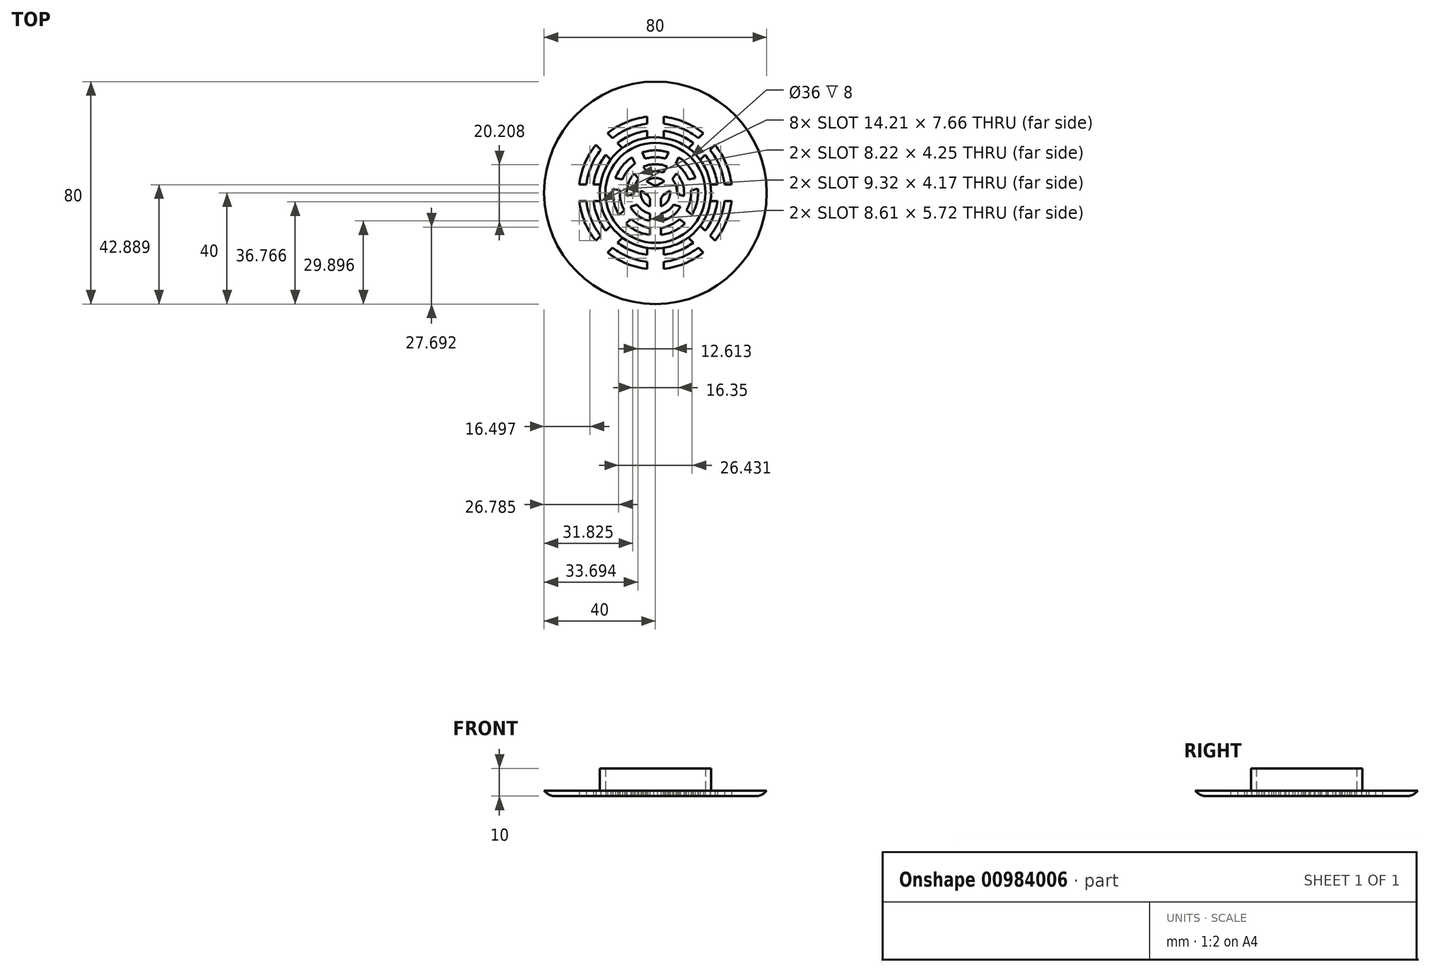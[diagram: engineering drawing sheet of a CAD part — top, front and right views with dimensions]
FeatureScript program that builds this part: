
annotation { "Feature Type Name" : "Feature", "Feature Type Description" : "" }
export const myFeature = defineFeature(function(context is Context, id is Id, definition is map)
    precondition{}
    {
        {
            var Q0;
            Q0=qCreatedBy(makeId("Top.planeOp"),FACE);
            var sketch = newSketch(context, id + "F0", { "sketchPlane" : qUnion([Q0])});
            skCircle(sketch, "E0", {"center": v(0, 0) * mm, "radius": 40 * mm});
            skCircle(sketch, "E1", {"center": v(0, 0) * mm, "radius": 20 * mm});
            skCircle(sketch, "E2.0", {"center": v(0, 0) * mm, "radius": 18 * mm});
            skSolve(sketch);
        }
        {
            var Q0;
            Q0=makeQuery(id+"F0.imprint","IMPRINT",FACE,{"disambiguationData":[TD([[makeQuery(id+"F0.imprint","IMPRINT",EDGE,{"derivedFrom":sQuery(id+"F0.wireOp",EDGE,"E0")}),1.0]])]});
            var Q1;
            Q1=makeQuery(id+"F0.imprint","IMPRINT",FACE,{"disambiguationData":[TD([[makeQuery(id+"F0.imprint","IMPRINT",EDGE,{"derivedFrom":sQuery(id+"F0.wireOp",EDGE,"E2.0")}),1.0]])]});
            var Q2;
            Q2=makeQuery(id+"F0.imprint","IMPRINT",FACE,{"disambiguationData":[TD([[makeQuery(id+"F0.imprint","IMPRINT",EDGE,{"derivedFrom":sQuery(id+"F0.wireOp",EDGE,"E1")}),1.0]])]});
            extrude(context, id + "F1", {"entities" : qUnion([Q0, Q1, Q2]), "depth" : 2 * mm, "offsetDistance" : 25 * mm});
        }
        {
            var Q0;
            Q0=makeQuery(id+"F0.imprint","IMPRINT",FACE,{"disambiguationData":[TD([[makeQuery(id+"F0.imprint","IMPRINT",EDGE,{"derivedFrom":sQuery(id+"F0.wireOp",EDGE,"E1")}),1.0]])]});
            extrude(context, id + "F2", {"entities" : qUnion([Q0]), "operationType" : NewBodyOperationType.ADD, "depth" : 10 * mm, "offsetDistance" : 25 * mm});
        }
        {
            var Q0;
            Q0=makeQuery(id+"F1.opExtrude","CAP_EDGE",EDGE,{"disambiguationData":[OSD([sQuery(id+"F0.wireOp",EDGE,"E0")])],"isStart":true});
            fillet(context, id + "F3", {"entities" : qUnion([Q0]), "radius" : 5 * mm, "tangentPropagation" : true, "allowEdgeOverflow" : false});
        }
        {
            var Q0;
            Q0=makeQuery(id+"F1.opExtrude","CAP_FACE",FACE,{"disambiguationData":[OSD([sQuery(id+"F0.wireOp",EDGE,"E0")])],"isStart":true});
            var sketch = newSketch(context, id + "F4", { "sketchPlane" : qUnion([Q0])});
            skCircle(sketch, "E3", {"center": v(0, 0) * mm, "radius": 22.5 * mm});
            skCircle(sketch, "E4.0", {"center": v(0, 0) * mm, "radius": 20 * mm});
            skLineSegment(sketch, "E5", {"start": v(-3, 22.3) * mm, "end": v(-3, 19.77) * mm});
            skLineSegment(sketch, "E6", {"start": v(3, 22.3) * mm, "end": v(3, 19.77) * mm});
            skLineSegment(sketch, "E7.1.0", {"start": v(-17.89, 13.65) * mm, "end": v(-16.1, 11.86) * mm});
            skLineSegment(sketch, "E7.1.2", {"start": v(-13.65, 17.89) * mm, "end": v(-11.86, 16.1) * mm});
            skLineSegment(sketch, "E7.2.0", {"start": v(-22.3, -3) * mm, "end": v(-19.77, -3) * mm});
            skLineSegment(sketch, "E7.2.2", {"start": v(-22.3, 3) * mm, "end": v(-19.77, 3) * mm});
            skLineSegment(sketch, "E7.3.0", {"start": v(-13.65, -17.89) * mm, "end": v(-11.86, -16.1) * mm});
            skLineSegment(sketch, "E7.3.2", {"start": v(-17.89, -13.65) * mm, "end": v(-16.1, -11.86) * mm});
            skLineSegment(sketch, "E7.4.0", {"start": v(3, -22.3) * mm, "end": v(3, -19.77) * mm});
            skLineSegment(sketch, "E7.4.2", {"start": v(-3, -22.3) * mm, "end": v(-3, -19.77) * mm});
            skLineSegment(sketch, "E7.5.0", {"start": v(17.89, -13.65) * mm, "end": v(16.1, -11.86) * mm});
            skLineSegment(sketch, "E7.5.2", {"start": v(13.65, -17.89) * mm, "end": v(11.86, -16.1) * mm});
            skLineSegment(sketch, "E7.6.0", {"start": v(22.3, 3) * mm, "end": v(19.77, 3) * mm});
            skLineSegment(sketch, "E7.6.2", {"start": v(22.3, -3) * mm, "end": v(19.77, -3) * mm});
            skLineSegment(sketch, "E7.7.0", {"start": v(13.65, 17.89) * mm, "end": v(11.86, 16.1) * mm});
            skLineSegment(sketch, "E7.7.2", {"start": v(17.89, 13.65) * mm, "end": v(16.1, 11.86) * mm});
            skCircle(sketch, "E8", {"center": v(0, 0) * mm, "radius": 25 * mm});
            skCircle(sketch, "E9", {"center": v(0, 0) * mm, "radius": 27.5 * mm});
            skLineSegment(sketch, "E10", {"start": v(-3, 27.34) * mm, "end": v(-3, 24.82) * mm});
            skLineSegment(sketch, "E11", {"start": v(3, 27.34) * mm, "end": v(3, 24.82) * mm});
            skLineSegment(sketch, "E12.1.0", {"start": v(-21.45, 17.2) * mm, "end": v(-19.67, 15.43) * mm});
            skLineSegment(sketch, "E12.1.2", {"start": v(-17.2, 21.45) * mm, "end": v(-15.43, 19.67) * mm});
            skLineSegment(sketch, "E12.2.0", {"start": v(-27.34, -3) * mm, "end": v(-24.82, -3) * mm});
            skLineSegment(sketch, "E12.2.2", {"start": v(-27.34, 3) * mm, "end": v(-24.82, 3) * mm});
            skLineSegment(sketch, "E12.3.0", {"start": v(-17.2, -21.45) * mm, "end": v(-15.43, -19.67) * mm});
            skLineSegment(sketch, "E12.3.2", {"start": v(-21.45, -17.2) * mm, "end": v(-19.67, -15.43) * mm});
            skLineSegment(sketch, "E12.4.0", {"start": v(3, -27.34) * mm, "end": v(3, -24.82) * mm});
            skLineSegment(sketch, "E12.4.2", {"start": v(-3, -27.34) * mm, "end": v(-3, -24.82) * mm});
            skLineSegment(sketch, "E12.5.0", {"start": v(21.45, -17.2) * mm, "end": v(19.67, -15.43) * mm});
            skLineSegment(sketch, "E12.5.2", {"start": v(17.2, -21.45) * mm, "end": v(15.43, -19.67) * mm});
            skLineSegment(sketch, "E12.6.0", {"start": v(27.34, 3) * mm, "end": v(24.82, 3) * mm});
            skLineSegment(sketch, "E12.6.2", {"start": v(27.34, -3) * mm, "end": v(24.82, -3) * mm});
            skLineSegment(sketch, "E12.7.0", {"start": v(17.2, 21.45) * mm, "end": v(15.43, 19.67) * mm});
            skLineSegment(sketch, "E12.7.2", {"start": v(21.45, 17.2) * mm, "end": v(19.67, 15.43) * mm});
            skSolve(sketch);
        }
        {
            var Q0;
            {var subQ0=sQuery(id+"F4.wireOp",EDGE,"E5");Q0=makeQuery(id+"F4.imprint","IMPRINT",FACE,{"disambiguationData":[TD([[makeQuery(id+"F4.imprint","IMPRINT",EDGE,{"derivedFrom":subQ0}),-1.0]])]});}
            var Q1;
            {var subQ0=sQuery(id+"F4.wireOp",EDGE,"E7.1.0");Q1=makeQuery(id+"F4.imprint","IMPRINT",FACE,{"disambiguationData":[TD([[makeQuery(id+"F4.imprint","IMPRINT",EDGE,{"derivedFrom":subQ0}),-1.0]])]});}
            var Q2;
            {var subQ0=sQuery(id+"F4.wireOp",EDGE,"E7.2.0");Q2=makeQuery(id+"F4.imprint","IMPRINT",FACE,{"disambiguationData":[TD([[makeQuery(id+"F4.imprint","IMPRINT",EDGE,{"derivedFrom":subQ0}),-1.0]])]});}
            var Q3;
            {var subQ0=sQuery(id+"F4.wireOp",EDGE,"E7.3.0");Q3=makeQuery(id+"F4.imprint","IMPRINT",FACE,{"disambiguationData":[TD([[makeQuery(id+"F4.imprint","IMPRINT",EDGE,{"derivedFrom":subQ0}),-1.0]])]});}
            var Q4;
            {var subQ0=sQuery(id+"F4.wireOp",EDGE,"E7.4.0");Q4=makeQuery(id+"F4.imprint","IMPRINT",FACE,{"disambiguationData":[TD([[makeQuery(id+"F4.imprint","IMPRINT",EDGE,{"derivedFrom":subQ0}),-1.0]])]});}
            var Q5;
            {var subQ0=sQuery(id+"F4.wireOp",EDGE,"E7.5.0");Q5=makeQuery(id+"F4.imprint","IMPRINT",FACE,{"disambiguationData":[TD([[makeQuery(id+"F4.imprint","IMPRINT",EDGE,{"derivedFrom":subQ0}),-1.0]])]});}
            var Q6;
            {var subQ0=sQuery(id+"F4.wireOp",EDGE,"E7.6.0");Q6=makeQuery(id+"F4.imprint","IMPRINT",FACE,{"disambiguationData":[TD([[makeQuery(id+"F4.imprint","IMPRINT",EDGE,{"derivedFrom":subQ0}),-1.0]])]});}
            var Q7;
            {var subQ0=sQuery(id+"F4.wireOp",EDGE,"E6");Q7=makeQuery(id+"F4.imprint","IMPRINT",FACE,{"disambiguationData":[TD([[makeQuery(id+"F4.imprint","IMPRINT",EDGE,{"derivedFrom":subQ0}),1.0]])]});}
            var Q8;
            {var subQ0=sQuery(id+"F4.wireOp",EDGE,"E10");Q8=makeQuery(id+"F4.imprint","IMPRINT",FACE,{"disambiguationData":[TD([[makeQuery(id+"F4.imprint","IMPRINT",EDGE,{"derivedFrom":subQ0}),-1.0]])]});}
            var Q9;
            {var subQ0=sQuery(id+"F4.wireOp",EDGE,"E11");Q9=makeQuery(id+"F4.imprint","IMPRINT",FACE,{"disambiguationData":[TD([[makeQuery(id+"F4.imprint","IMPRINT",EDGE,{"derivedFrom":subQ0}),1.0]])]});}
            var Q10;
            {var subQ0=sQuery(id+"F4.wireOp",EDGE,"E12.6.0");Q10=makeQuery(id+"F4.imprint","IMPRINT",FACE,{"disambiguationData":[TD([[makeQuery(id+"F4.imprint","IMPRINT",EDGE,{"derivedFrom":subQ0}),-1.0]])]});}
            var Q11;
            {var subQ0=sQuery(id+"F4.wireOp",EDGE,"E12.5.0");Q11=makeQuery(id+"F4.imprint","IMPRINT",FACE,{"disambiguationData":[TD([[makeQuery(id+"F4.imprint","IMPRINT",EDGE,{"derivedFrom":subQ0}),-1.0]])]});}
            var Q12;
            {var subQ0=sQuery(id+"F4.wireOp",EDGE,"E12.4.0");Q12=makeQuery(id+"F4.imprint","IMPRINT",FACE,{"disambiguationData":[TD([[makeQuery(id+"F4.imprint","IMPRINT",EDGE,{"derivedFrom":subQ0}),-1.0]])]});}
            var Q13;
            {var subQ0=sQuery(id+"F4.wireOp",EDGE,"E12.3.0");Q13=makeQuery(id+"F4.imprint","IMPRINT",FACE,{"disambiguationData":[TD([[makeQuery(id+"F4.imprint","IMPRINT",EDGE,{"derivedFrom":subQ0}),-1.0]])]});}
            var Q14;
            {var subQ0=sQuery(id+"F4.wireOp",EDGE,"E12.2.0");Q14=makeQuery(id+"F4.imprint","IMPRINT",FACE,{"disambiguationData":[TD([[makeQuery(id+"F4.imprint","IMPRINT",EDGE,{"derivedFrom":subQ0}),-1.0]])]});}
            var Q15;
            {var subQ0=sQuery(id+"F4.wireOp",EDGE,"E12.1.0");Q15=makeQuery(id+"F4.imprint","IMPRINT",FACE,{"disambiguationData":[TD([[makeQuery(id+"F4.imprint","IMPRINT",EDGE,{"derivedFrom":subQ0}),-1.0]])]});}
            extrude(context, id + "F5", {"entities" : qUnion([Q0, Q1, Q2, Q3, Q4, Q5, Q6, Q7, Q8, Q9, Q10, Q11, Q12, Q13, Q14, Q15]), "operationType" : NewBodyOperationType.REMOVE, "endBound" : BoundingType.THROUGH_ALL, "oppositeDirection" : true, "depth" : 25 * mm, "offsetDistance" : 25 * mm});
        }
        {
            var Q0;
            Q0=makeQuery(id+"F0.imprint","IMPRINT",FACE,{"disambiguationData":[TD([[makeQuery(id+"F0.imprint","IMPRINT",EDGE,{"derivedFrom":sQuery(id+"F0.wireOp",EDGE,"E2.0")}),1.0]])]});
            var sketch = newSketch(context, id + "F6", { "sketchPlane" : qUnion([Q0])});
            skCircle(sketch, "E13.0", {"center": v(0, 0) * mm, "radius": 18 * mm});
            skCircle(sketch, "E14", {"center": v(0, 0) * mm, "radius": 2.8 * mm, "construction": true});
            skCircle(sketch, "E15", {"center": v(0, 0) * mm, "radius": 15.3 * mm});
            skCircle(sketch, "E16", {"center": v(0, 0) * mm, "radius": 5.3 * mm, "construction": true});
            skLineSegment(sketch, "E17", {"start": v(-2, -4.9) * mm, "end": v(-2, -1.96) * mm});
            skLineSegment(sketch, "E18", {"start": v(2, -4.9) * mm, "end": v(2, -1.96) * mm});
            skLineSegment(sketch, "E19.1.0", {"start": v(5.25, 0.72) * mm, "end": v(2.7, -0.75) * mm});
            skLineSegment(sketch, "E19.1.2", {"start": v(3.25, 4.19) * mm, "end": v(0.7, 2.71) * mm});
            skCircle(sketch, "E19.1.3", {"center": v(0, 0) * mm, "radius": 2.8 * mm});
            skLineSegment(sketch, "E19.2.0", {"start": v(-3.25, 4.19) * mm, "end": v(-0.7, 2.71) * mm});
            skCircle(sketch, "E19.2.1", {"center": v(0, 0) * mm, "radius": 5.3 * mm});
            skLineSegment(sketch, "E19.2.2", {"start": v(-5.25, 0.72) * mm, "end": v(-2.7, -0.75) * mm});
            skCircle(sketch, "E20", {"center": v(0, 0) * mm, "radius": 7.8 * mm});
            skCircle(sketch, "E21", {"center": v(0, 0) * mm, "radius": 10.3 * mm});
            skLineSegment(sketch, "E22", {"start": v(-2, -10.1) * mm, "end": v(-2, -7.54) * mm});
            skLineSegment(sketch, "E23", {"start": v(2, -7.54) * mm, "end": v(2, -10.1) * mm});
            skLineSegment(sketch, "E24.1.0", {"start": v(9, -5.02) * mm, "end": v(6.55, -4.23) * mm});
            skLineSegment(sketch, "E24.1.1", {"start": v(7.79, -0.43) * mm, "end": v(10.23, -1.22) * mm});
            skLineSegment(sketch, "E24.2.0", {"start": v(7.56, 7) * mm, "end": v(6.05, 4.92) * mm});
            skLineSegment(sketch, "E24.2.1", {"start": v(2.81, 7.28) * mm, "end": v(4.32, 9.35) * mm});
            skLineSegment(sketch, "E24.3.0", {"start": v(-4.32, 9.35) * mm, "end": v(-2.81, 7.28) * mm});
            skLineSegment(sketch, "E24.3.1", {"start": v(-6.05, 4.92) * mm, "end": v(-7.56, 7) * mm});
            skLineSegment(sketch, "E24.4.0", {"start": v(-10.23, -1.22) * mm, "end": v(-7.79, -0.43) * mm});
            skLineSegment(sketch, "E24.4.1", {"start": v(-6.55, -4.23) * mm, "end": v(-9, -5.02) * mm});
            skCircle(sketch, "E25", {"center": v(0, 0) * mm, "radius": 12.8 * mm});
            skLineSegment(sketch, "E26", {"start": v(-2, -12.64) * mm, "end": v(-2, -15.17) * mm});
            skLineSegment(sketch, "E27", {"start": v(2, -12.64) * mm, "end": v(2, -15.17) * mm});
            skLineSegment(sketch, "E28.1.0", {"start": v(11.13, -6.32) * mm, "end": v(13.1, -7.9) * mm});
            skLineSegment(sketch, "E28.1.1", {"start": v(8.64, -9.45) * mm, "end": v(10.61, -11.02) * mm});
            skLineSegment(sketch, "E28.2.0", {"start": v(11.88, 4.76) * mm, "end": v(14.34, 5.33) * mm});
            skLineSegment(sketch, "E28.2.1", {"start": v(12.77, 0.86) * mm, "end": v(15.23, 1.43) * mm});
            skLineSegment(sketch, "E28.3.0", {"start": v(3.68, 12.26) * mm, "end": v(4.78, 14.53) * mm});
            skLineSegment(sketch, "E28.3.1", {"start": v(7.29, 10.52) * mm, "end": v(8.38, 12.8) * mm});
            skLineSegment(sketch, "E28.4.0", {"start": v(-7.29, 10.52) * mm, "end": v(-8.38, 12.8) * mm});
            skLineSegment(sketch, "E28.4.1", {"start": v(-3.68, 12.26) * mm, "end": v(-4.78, 14.53) * mm});
            skLineSegment(sketch, "E28.5.0", {"start": v(-12.77, 0.86) * mm, "end": v(-15.23, 1.43) * mm});
            skLineSegment(sketch, "E28.5.1", {"start": v(-11.88, 4.76) * mm, "end": v(-14.34, 5.33) * mm});
            skLineSegment(sketch, "E28.6.0", {"start": v(-8.64, -9.45) * mm, "end": v(-10.61, -11.02) * mm});
            skLineSegment(sketch, "E28.6.1", {"start": v(-11.13, -6.32) * mm, "end": v(-13.1, -7.9) * mm});
            skSolve(sketch);
        }
        {
            var Q0;
            {var subQ0=sQuery(id+"F6.wireOp",EDGE,"E17");Q0=makeQuery(id+"F6.imprint","IMPRINT",FACE,{"disambiguationData":[TD([[makeQuery(id+"F6.imprint","IMPRINT",EDGE,{"derivedFrom":subQ0}),1.0]])]});}
            var Q1;
            {var subQ0=sQuery(id+"F6.wireOp",EDGE,"E18");Q1=makeQuery(id+"F6.imprint","IMPRINT",FACE,{"disambiguationData":[TD([[makeQuery(id+"F6.imprint","IMPRINT",EDGE,{"derivedFrom":subQ0}),-1.0]])]});}
            var Q2;
            {var subQ0=sQuery(id+"F6.wireOp",EDGE,"E19.1.2");Q2=makeQuery(id+"F6.imprint","IMPRINT",FACE,{"disambiguationData":[TD([[makeQuery(id+"F6.imprint","IMPRINT",EDGE,{"derivedFrom":subQ0}),-1.0]])]});}
            var Q3;
            {var subQ0=sQuery(id+"F6.wireOp",EDGE,"E23");Q3=makeQuery(id+"F6.imprint","IMPRINT",FACE,{"disambiguationData":[TD([[makeQuery(id+"F6.imprint","IMPRINT",EDGE,{"derivedFrom":subQ0}),1.0]])]});}
            var Q4;
            {var subQ0=sQuery(id+"F6.wireOp",EDGE,"E24.1.1");Q4=makeQuery(id+"F6.imprint","IMPRINT",FACE,{"disambiguationData":[TD([[makeQuery(id+"F6.imprint","IMPRINT",EDGE,{"derivedFrom":subQ0}),1.0]])]});}
            var Q5;
            {var subQ0=sQuery(id+"F6.wireOp",EDGE,"E24.2.1");Q5=makeQuery(id+"F6.imprint","IMPRINT",FACE,{"disambiguationData":[TD([[makeQuery(id+"F6.imprint","IMPRINT",EDGE,{"derivedFrom":subQ0}),1.0]])]});}
            var Q6;
            {var subQ0=sQuery(id+"F6.wireOp",EDGE,"E24.3.1");Q6=makeQuery(id+"F6.imprint","IMPRINT",FACE,{"disambiguationData":[TD([[makeQuery(id+"F6.imprint","IMPRINT",EDGE,{"derivedFrom":subQ0}),1.0]])]});}
            var Q7;
            {var subQ0=sQuery(id+"F6.wireOp",EDGE,"E22");Q7=makeQuery(id+"F6.imprint","IMPRINT",FACE,{"disambiguationData":[TD([[makeQuery(id+"F6.imprint","IMPRINT",EDGE,{"derivedFrom":subQ0}),1.0]])]});}
            var Q8;
            {var subQ0=sQuery(id+"F6.wireOp",EDGE,"E26");Q8=makeQuery(id+"F6.imprint","IMPRINT",FACE,{"disambiguationData":[TD([[makeQuery(id+"F6.imprint","IMPRINT",EDGE,{"derivedFrom":subQ0}),-1.0]])]});}
            var Q9;
            {var subQ0=sQuery(id+"F6.wireOp",EDGE,"E27");Q9=makeQuery(id+"F6.imprint","IMPRINT",FACE,{"disambiguationData":[TD([[makeQuery(id+"F6.imprint","IMPRINT",EDGE,{"derivedFrom":subQ0}),1.0]])]});}
            var Q10;
            {var subQ0=sQuery(id+"F6.wireOp",EDGE,"E28.1.0");Q10=makeQuery(id+"F6.imprint","IMPRINT",FACE,{"disambiguationData":[TD([[makeQuery(id+"F6.imprint","IMPRINT",EDGE,{"derivedFrom":subQ0}),1.0]])]});}
            var Q11;
            {var subQ0=sQuery(id+"F6.wireOp",EDGE,"E28.2.0");Q11=makeQuery(id+"F6.imprint","IMPRINT",FACE,{"disambiguationData":[TD([[makeQuery(id+"F6.imprint","IMPRINT",EDGE,{"derivedFrom":subQ0}),1.0]])]});}
            var Q12;
            {var subQ0=sQuery(id+"F6.wireOp",EDGE,"E28.3.0");Q12=makeQuery(id+"F6.imprint","IMPRINT",FACE,{"disambiguationData":[TD([[makeQuery(id+"F6.imprint","IMPRINT",EDGE,{"derivedFrom":subQ0}),1.0]])]});}
            var Q13;
            {var subQ0=sQuery(id+"F6.wireOp",EDGE,"E28.4.0");Q13=makeQuery(id+"F6.imprint","IMPRINT",FACE,{"disambiguationData":[TD([[makeQuery(id+"F6.imprint","IMPRINT",EDGE,{"derivedFrom":subQ0}),1.0]])]});}
            var Q14;
            {var subQ0=sQuery(id+"F6.wireOp",EDGE,"E28.5.0");Q14=makeQuery(id+"F6.imprint","IMPRINT",FACE,{"disambiguationData":[TD([[makeQuery(id+"F6.imprint","IMPRINT",EDGE,{"derivedFrom":subQ0}),1.0]])]});}
            extrude(context, id + "F7", {"entities" : qUnion([Q0, Q1, Q2, Q3, Q4, Q5, Q6, Q7, Q8, Q9, Q10, Q11, Q12, Q13, Q14]), "operationType" : NewBodyOperationType.REMOVE, "endBound" : BoundingType.THROUGH_ALL, "depth" : 25 * mm, "offsetDistance" : 25 * mm});
        }
    });
